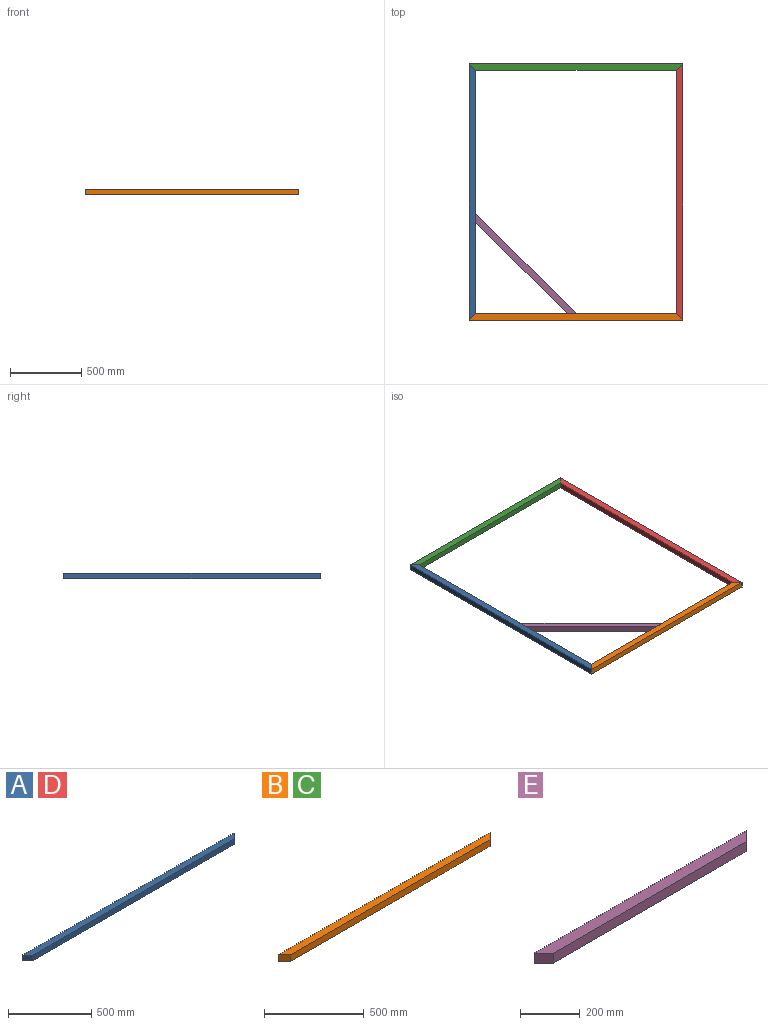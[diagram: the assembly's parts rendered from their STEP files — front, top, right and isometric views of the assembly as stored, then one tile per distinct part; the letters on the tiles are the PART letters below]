
ASSEMBLY  parts=5 mates=5
PART A: 6 faces, bbox 1800x45x40 mm
  f0: plane 45x45mm, normal (0.71,-0.71,0), area 2545.6mm2, adj f1,f3,f4,f5
  f1: plane 1800x40mm, normal (0,1,0), area 72000mm2, adj f0,f2,f4,f5
  f2: plane 45x45mm, normal (-0.71,-0.71,0), area 2545.6mm2, adj f1,f3,f4,f5
  f3: plane 1710x40mm, normal (0,-1,0), area 68400mm2, adj f0,f2,f4,f5
  f4: plane 1800x45mm, normal (0,0,1), area 78975mm2, adj f0,f1,f2,f3
  f5: plane 1800x45mm, normal (0,0,-1), area 78975mm2, adj f0,f1,f2,f3
PART B: 6 faces, bbox 1500x45x40 mm
  f0: plane 45x45mm, normal (0.71,-0.71,0), area 2545.6mm2, adj f1,f3,f4,f5
  f1: plane 1500x40mm, normal (0,1,0), area 60000mm2, adj f0,f2,f4,f5
  f2: plane 45x45mm, normal (-0.71,-0.71,0), area 2545.6mm2, adj f1,f3,f4,f5
  f3: plane 1410x40mm, normal (0,-1,0), area 56400mm2, adj f0,f2,f4,f5
  f4: plane 1500x45mm, normal (0,0,1), area 65475mm2, adj f0,f1,f2,f3
  f5: plane 1500x45mm, normal (0,0,-1), area 65475mm2, adj f0,f1,f2,f3
PART C: same geometry as B
PART D: same geometry as A
PART E: 6 faces, bbox 1000x45x40 mm
  f0: plane 1000x40mm, normal (0,1,0), area 40000mm2, adj f1,f3,f4,f5
  f1: plane 45x45mm, normal (-0.71,-0.71,0), area 2545.6mm2, adj f0,f2,f4,f5
  f2: plane 910x40mm, normal (0,-1,0), area 36400mm2, adj f1,f3,f4,f5
  f3: plane 45x45mm, normal (0.71,-0.71,0), area 2545.6mm2, adj f0,f2,f4,f5
  f4: plane 1000x45mm, normal (0,0,1), area 42975mm2, adj f0,f1,f2,f3
  f5: plane 1000x45mm, normal (0,0,-1), area 42975mm2, adj f0,f1,f2,f3
PLACE A rot(axis=(0,0,1),90deg) t=(-2082.23,979.63,6.01)mm
PLACE B rot(axis=(0,0,1),180deg) t=(-2008.96,-644.26,6.01)mm
PLACE C t=(-792.28,1072.76,6.01)mm
PLACE D rot(axis=(0,0,-1),90deg) t=(-719.01,-551.12,6.01)mm
PLACE E rot(axis=(0,0,-1),45deg) t=(-2021.9,-17.36,6.01)mm
MATE planar E.f1 <-> A.f3  axis (-1,0,0) through (-2105.62,34.54,26.01)mm
MATE fastened B.f2 <-> D.f0  axis (0.71,0.71,0) through (-673.12,-663.25,26.01)mm
MATE planar B.f3 <-> E.f3  axis (0,1,0) through (-1400.62,-640.75,26.01)mm
MATE fastened A.f2 <-> B.f0  axis (0.71,-0.71,0) through (-2128.12,-663.25,26.01)mm
MATE fastened A.f0 <-> C.f2  axis (0.71,0.71,0) through (-2128.12,1091.75,26.01)mm
